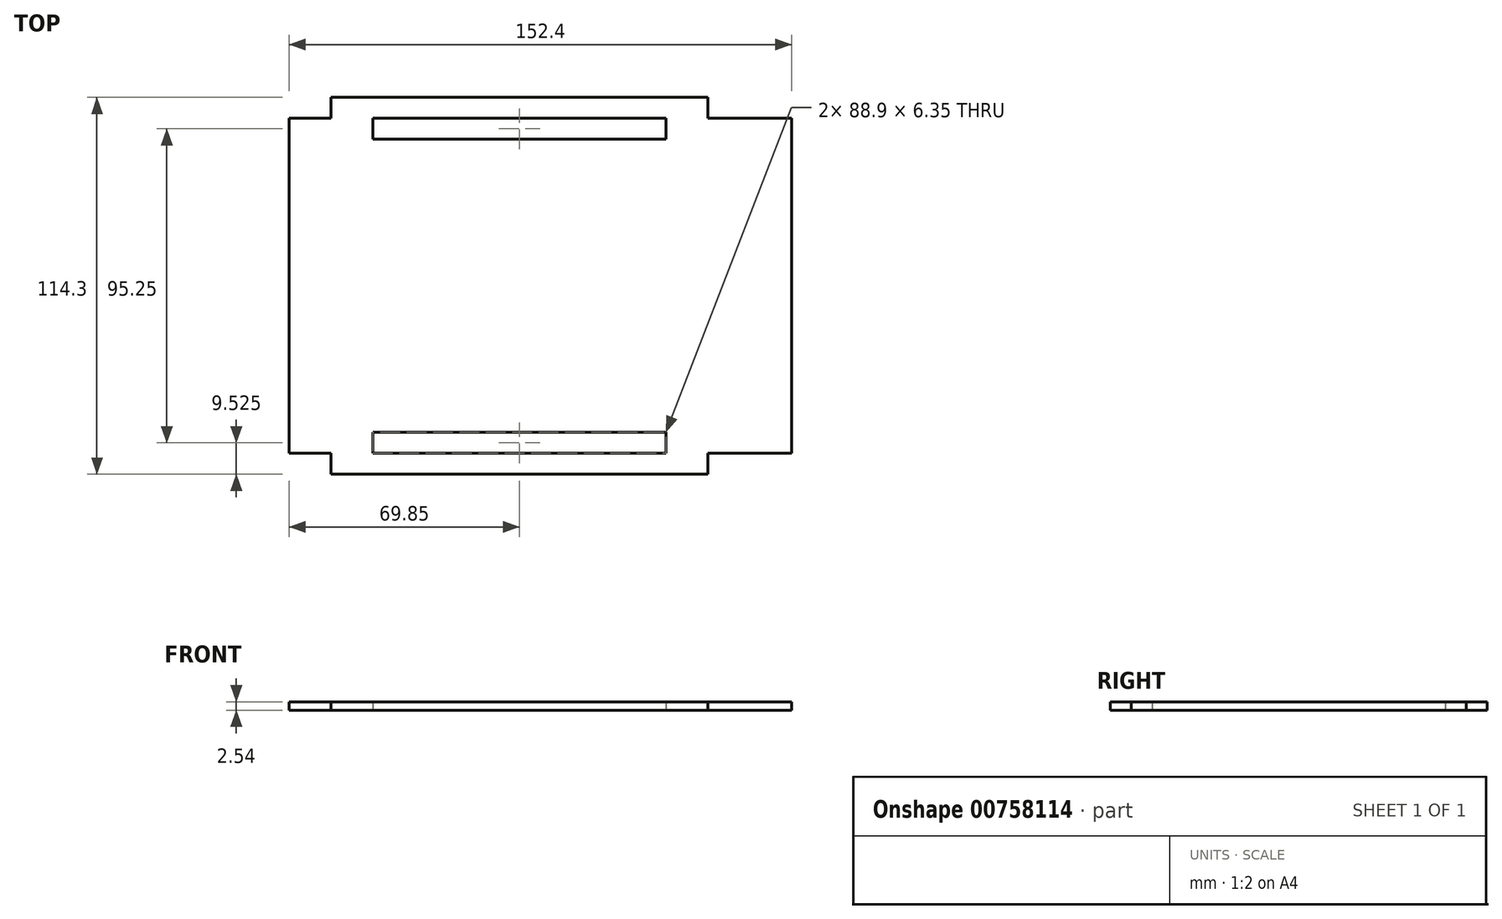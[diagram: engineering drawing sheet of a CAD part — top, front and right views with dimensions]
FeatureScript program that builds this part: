
annotation { "Feature Type Name" : "Feature", "Feature Type Description" : "" }
export const myFeature = defineFeature(function(context is Context, id is Id, definition is map)
    precondition{}
    {
        {
            var Q0;
            Q0=qCreatedBy(makeId("Top.planeOp"),FACE);
            var sketch = newSketch(context, id + "F0", { "sketchPlane" : qUnion([Q0])});
            skLineSegment(sketch, "E0", {"start": v(-76.2, 0) * mm, "end": v(-76.2, 50.8) * mm});
            skLineSegment(sketch, "E1", {"start": v(76.2, 0) * mm, "end": v(76.2, 50.8) * mm});
            skLineSegment(sketch, "E2", {"start": v(-76.2, 0) * mm, "end": v(-76.2, -50.8) * mm});
            skLineSegment(sketch, "E3", {"start": v(76.2, 0) * mm, "end": v(76.2, -50.8) * mm});
            skLineSegment(sketch, "E4", {"start": v(-76.2, -50.8) * mm, "end": v(76.2, -50.8) * mm});
            skLineSegment(sketch, "E5", {"start": v(-76.2, 50.8) * mm, "end": v(76.2, 50.8) * mm});
            skPoint(sketch, "E6", {"position": v(-50.8, -50.8) * mm});
            skPoint(sketch, "E7", {"position": v(38.1, -50.8) * mm});
            skLineSegment(sketch, "E8", {"start": v(-50.8, -50.8) * mm, "end": v(-50.8, -44.45) * mm});
            skLineSegment(sketch, "E9", {"start": v(-50.8, -44.45) * mm, "end": v(38.1, -44.45) * mm});
            skLineSegment(sketch, "E10", {"start": v(38.1, -44.45) * mm, "end": v(38.1, -50.8) * mm});
            skPoint(sketch, "E11", {"position": v(-50.8, 50.8) * mm});
            skPoint(sketch, "E12", {"position": v(38.1, 50.8) * mm});
            skLineSegment(sketch, "E13", {"start": v(-50.8, 50.8) * mm, "end": v(-50.8, 44.45) * mm});
            skLineSegment(sketch, "E14", {"start": v(-50.8, 44.45) * mm, "end": v(38.1, 44.45) * mm});
            skLineSegment(sketch, "E15", {"start": v(38.1, 50.8) * mm, "end": v(38.1, 44.45) * mm});
            skPoint(sketch, "E16", {"position": v(-63.5, -50.8) * mm});
            skPoint(sketch, "E17", {"position": v(50.8, -50.8) * mm});
            skPoint(sketch, "E18", {"position": v(-63.5, 50.8) * mm});
            skPoint(sketch, "E19", {"position": v(50.8, 50.8) * mm});
            skLineSegment(sketch, "E20", {"start": v(-63.5, -50.8) * mm, "end": v(-63.5, -57.15) * mm});
            skLineSegment(sketch, "E21", {"start": v(-63.5, 50.8) * mm, "end": v(-63.5, 57.15) * mm});
            skLineSegment(sketch, "E22", {"start": v(50.8, 50.8) * mm, "end": v(50.8, 57.15) * mm});
            skLineSegment(sketch, "E23", {"start": v(50.8, -50.8) * mm, "end": v(50.8, -57.15) * mm});
            skLineSegment(sketch, "E24", {"start": v(-63.5, 57.15) * mm, "end": v(50.8, 57.15) * mm});
            skLineSegment(sketch, "E25", {"start": v(-63.5, -57.15) * mm, "end": v(50.8, -57.15) * mm});
            skSolve(sketch);
        }
        {
            var Q0;
            {var subQ3=sQuery(id+"F0.wireOp",EDGE,"E0");Q0=makeQuery(id+"F0.imprint","IMPRINT",FACE,{"disambiguationData":[TD([[makeQuery(id+"F0.imprint","IMPRINT",EDGE,{"derivedFrom":subQ3}),-1.0]])]});}
            var Q1;
            {var subQ3=sQuery(id+"F0.wireOp",EDGE,"E21");Q1=makeQuery(id+"F0.imprint","IMPRINT",FACE,{"disambiguationData":[TD([[makeQuery(id+"F0.imprint","IMPRINT",EDGE,{"derivedFrom":subQ3}),-1.0]])]});}
            var Q2;
            {var subQ4=sQuery(id+"F0.wireOp",EDGE,"E20");Q2=makeQuery(id+"F0.imprint","IMPRINT",FACE,{"disambiguationData":[TD([[makeQuery(id+"F0.imprint","IMPRINT",EDGE,{"derivedFrom":subQ4}),1.0]])]});}
            extrude(context, id + "F1", {"entities" : qUnion([Q0, Q1, Q2]), "depth" : 2.54 * mm, "offsetDistance" : 25.4 * mm});
        }
    });
